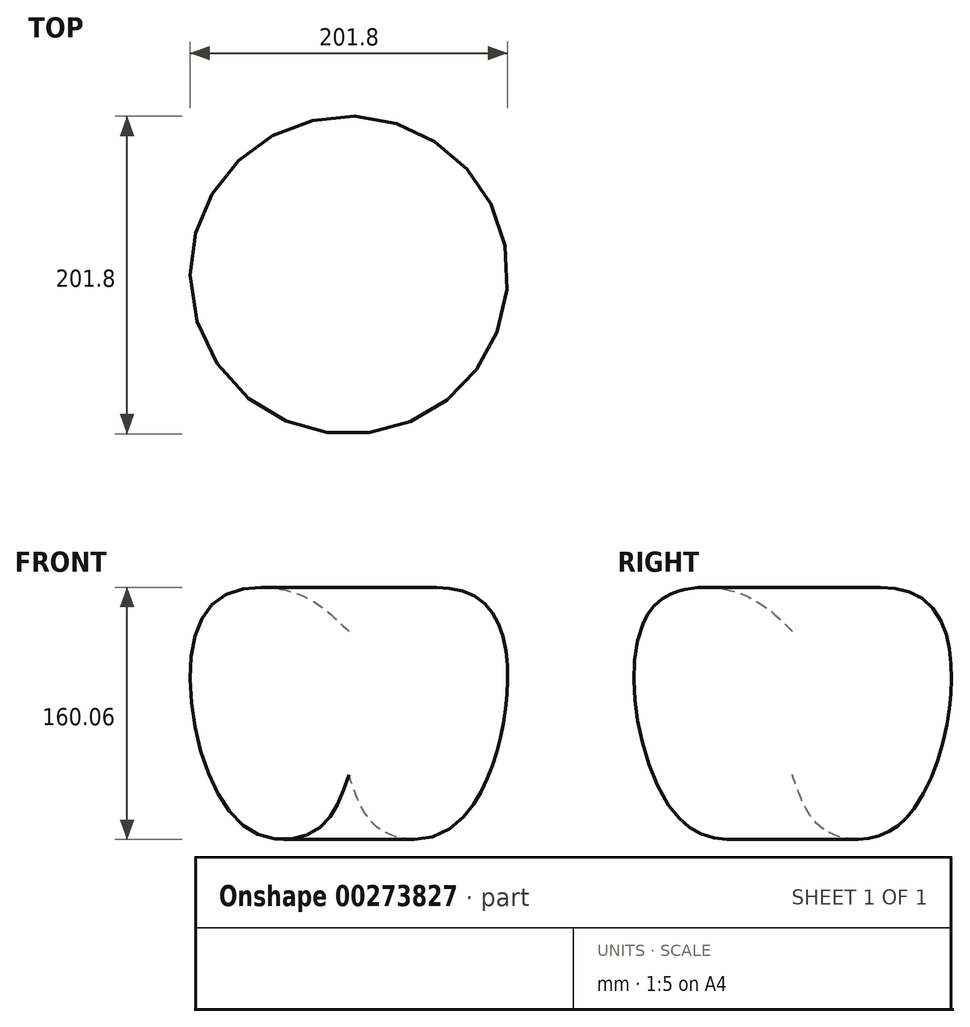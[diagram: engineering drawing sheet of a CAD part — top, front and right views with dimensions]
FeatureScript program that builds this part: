
annotation { "Feature Type Name" : "Feature", "Feature Type Description" : "" }
export const myFeature = defineFeature(function(context is Context, id is Id, definition is map)
    precondition{}
    {
        {
            var Q0;
            Q0=qCreatedBy(makeId("Front.planeOp"),FACE);
            var sketch = newSketch(context, id + "F0", { "sketchPlane" : qUnion([Q0])});
            skFitSpline(sketch, "E0", {"points": [v(0, -38.83) * mm, v(-19.53, -73.19) * mm, v(-62.83, -73.9) * mm, v(-99.07, 0) * mm, v(-85.42, 70.83) * mm, v(-34.12, 76.72) * mm, v(0, 52.24) * mm], "startDerivative": vector(-93.32, -282.19) * mm, "endDerivative": vector(199.3, -198.57) * mm});
            skLineSegment(sketch, "E1", {"start": v(0, 52.24) * mm, "end": v(0, -38.83) * mm});
            skSolve(sketch);
        }
        {
            var Q0;
            Q0=makeQuery(id+"F0.imprint","IMPRINT",FACE,{"disambiguationData":[TD([[makeQuery(id+"F0.imprint","IMPRINT",EDGE,{"derivedFrom":sQuery(id+"F0.wireOp",EDGE,"E0")}),-1.0]])]});
            var Q1;
            Q1=sQuery(id+"F0.wireOp",EDGE,"E1");
            revolve(context, id + "F1", {"entities" : qUnion([Q0]), "axis" : qUnion([Q1]), "revolveType" : RevolveType.FULL});
        }
    });
